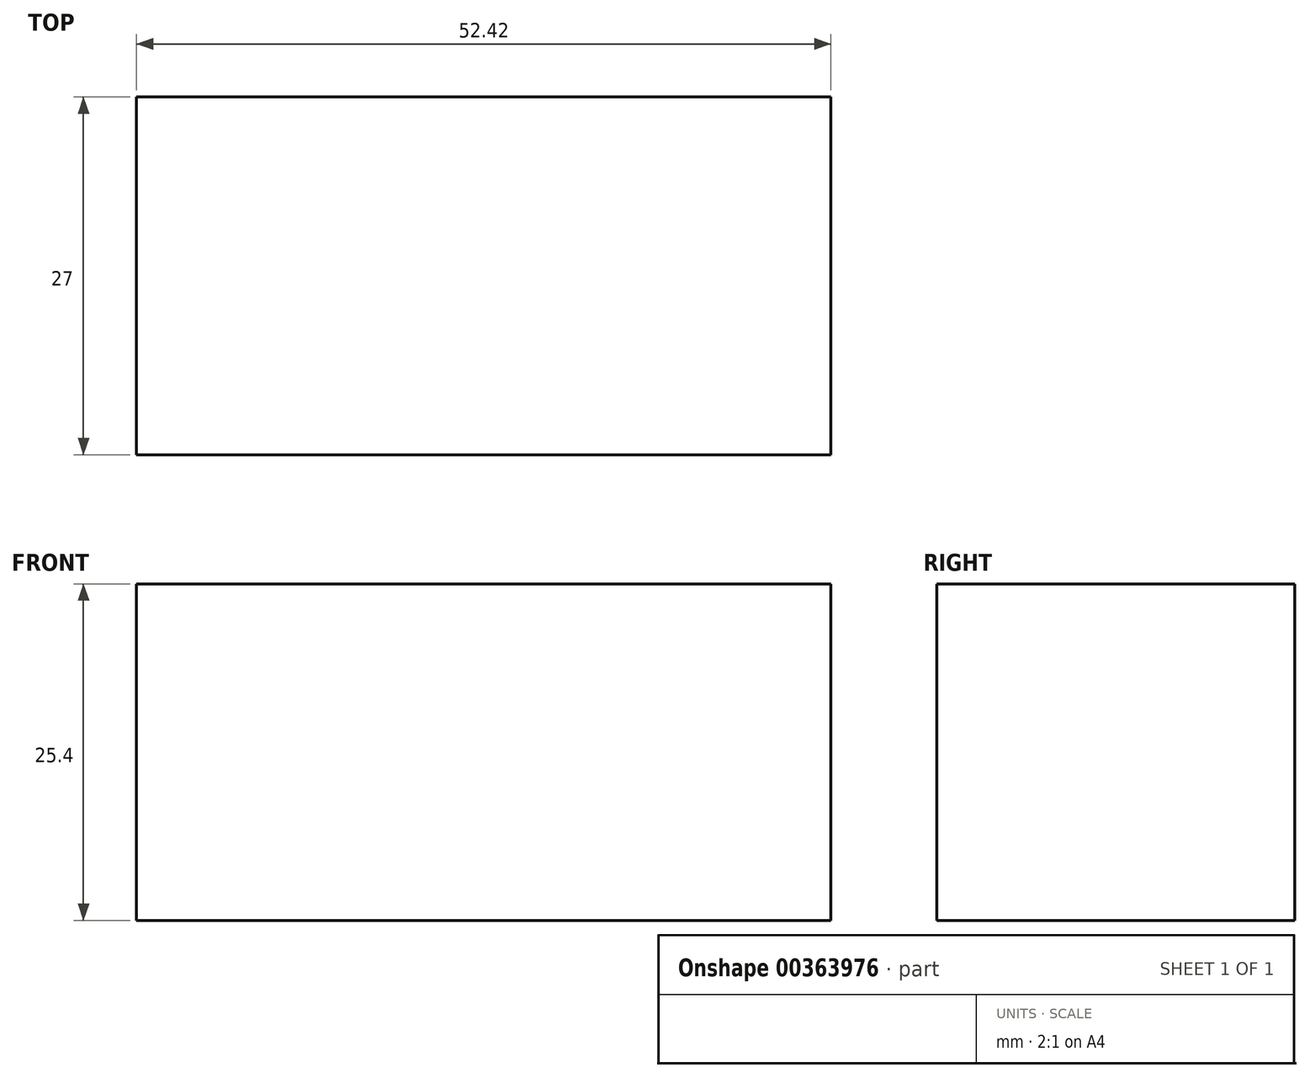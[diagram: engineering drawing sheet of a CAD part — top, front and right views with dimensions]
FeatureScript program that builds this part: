
annotation { "Feature Type Name" : "Feature", "Feature Type Description" : "" }
export const myFeature = defineFeature(function(context is Context, id is Id, definition is map)
    precondition{}
    {
        {
            var Q0;
            Q0=qCreatedBy(makeId("Top.planeOp"),FACE);
            var sketch = newSketch(context, id + "F0", { "sketchPlane" : qUnion([Q0])});
            skLineSegment(sketch, "E0.bottom", {"start": v(0, 0) * mm, "end": v(52.42, 0) * mm});
            skLineSegment(sketch, "E0.top", {"start": v(0, 27) * mm, "end": v(52.42, 27) * mm});
            skLineSegment(sketch, "E0.left", {"start": v(0, 0) * mm, "end": v(0, 27) * mm});
            skLineSegment(sketch, "E0.right", {"start": v(52.42, 0) * mm, "end": v(52.42, 27) * mm});
            skSolve(sketch);
        }
        {
            var Q0;
            Q0 = qSketchRegion(id + "F0", true);
            extrude(context, id + "F1", {"entities" : qUnion([Q0]), "depth" : 25.4 * mm});
        }
    });
